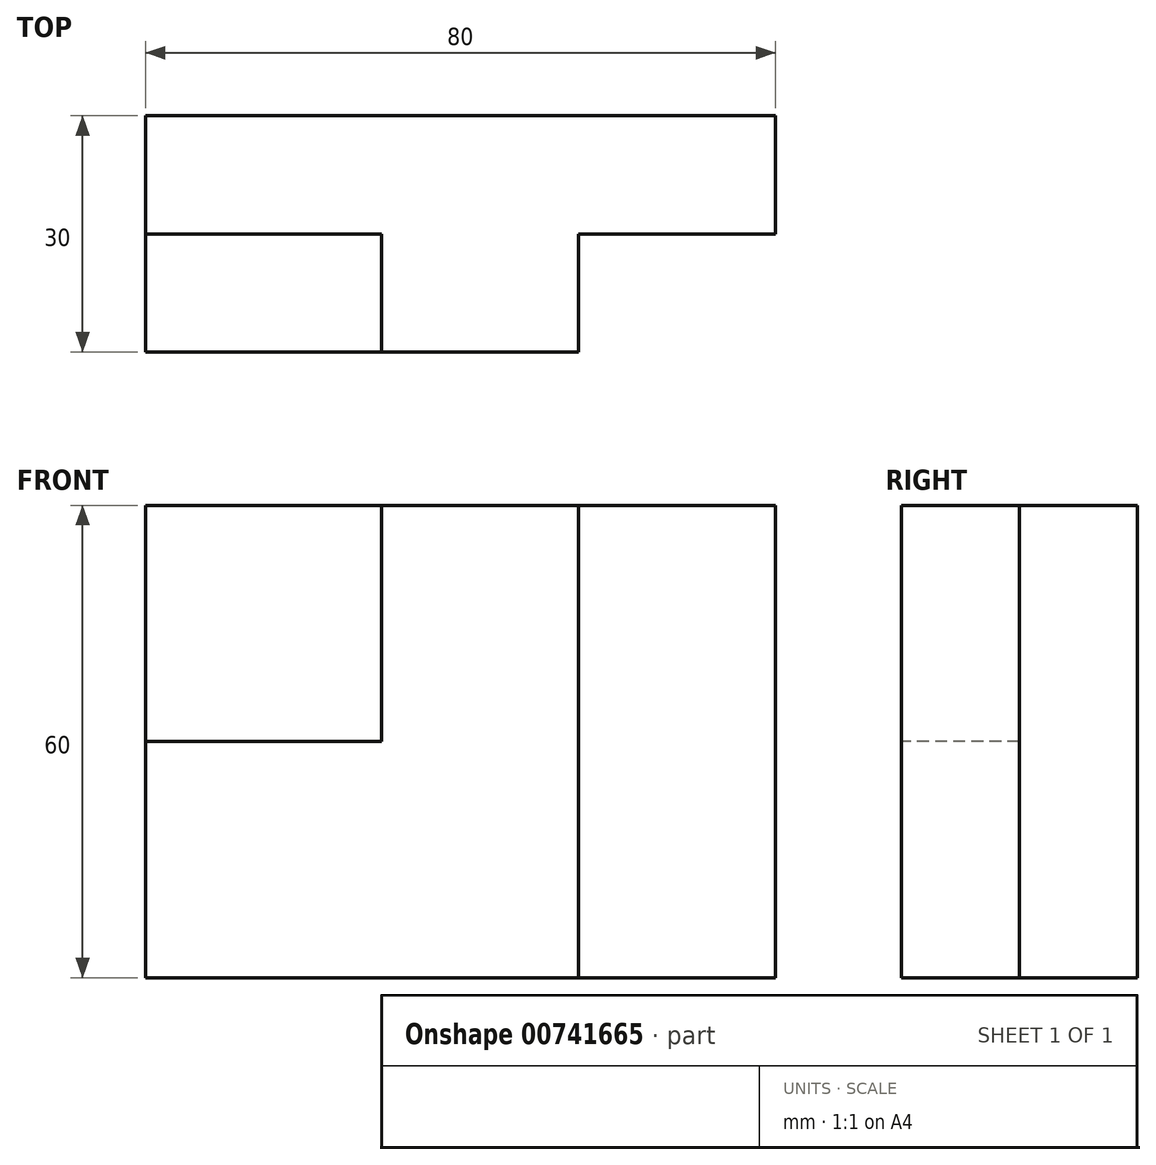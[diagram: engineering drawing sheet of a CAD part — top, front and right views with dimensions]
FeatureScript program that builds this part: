
annotation { "Feature Type Name" : "Feature", "Feature Type Description" : "" }
export const myFeature = defineFeature(function(context is Context, id is Id, definition is map)
    precondition{}
    {
        {
            var Q0;
            Q0=qCreatedBy(makeId("Front.planeOp"),FACE);
            var sketch = newSketch(context, id + "F0", { "sketchPlane" : qUnion([Q0])});
            skLineSegment(sketch, "E0", {"start": v(0, 0) * mm, "end": v(0, 60) * mm});
            skLineSegment(sketch, "E1", {"start": v(0, 60) * mm, "end": v(80, 60) * mm});
            skLineSegment(sketch, "E2", {"start": v(80, 60) * mm, "end": v(80, 0) * mm});
            skLineSegment(sketch, "E3", {"start": v(80, 0) * mm, "end": v(0, 0) * mm});
            skLineSegment(sketch, "E4", {"start": v(30, 60) * mm, "end": v(30, 30) * mm});
            skLineSegment(sketch, "E5", {"start": v(30, 30) * mm, "end": v(0, 30) * mm});
            skLineSegment(sketch, "E6", {"start": v(55, 60) * mm, "end": v(55, 0) * mm});
            skSolve(sketch);
        }
        {
            var Q0;
            Q0 = qSketchRegion(id + "F0", true);
            extrude(context, id + "F1", {"entities" : qUnion([Q0]), "depth" : -30 * mm, "offsetDistance" : 25 * mm});
        }
        {
            var Q0;
            {var subQ4=sQuery(id+"F0.wireOp",EDGE,"E4");Q0=makeQuery(id+"F0.imprint","IMPRINT",FACE,{"disambiguationData":[TD([[makeQuery(id+"F0.imprint","IMPRINT",EDGE,{"derivedFrom":subQ4}),-1.0]])]});}
            var Q1;
            {var subQ0=sQuery(id+"F0.wireOp",EDGE,"E2");Q1=makeQuery(id+"F0.imprint","IMPRINT",FACE,{"disambiguationData":[TD([[makeQuery(id+"F0.imprint","IMPRINT",EDGE,{"derivedFrom":subQ0}),-1.0]])]});}
            extrude(context, id + "F2", {"entities" : qUnion([Q0, Q1]), "operationType" : NewBodyOperationType.REMOVE, "oppositeDirection" : true, "depth" : 15 * mm, "offsetDistance" : 25 * mm});
        }
    });
